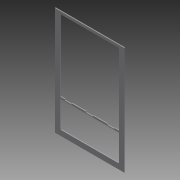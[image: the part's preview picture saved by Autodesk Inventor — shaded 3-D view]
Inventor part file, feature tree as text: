
AUTODESK INVENTOR PART (.ipt)
format: ipt  version: 2011 (Build 150239000, 239)  size: 1,064,960 bytes
history: native  units: in
note: dims shown in document units (in); Inventor stores cm internally (conversion verified against a paired STEP export)
features: extrude x29, sketch x29, fillet x4
ambient origin geometry x8: Origin, YZ Plane, XZ Plane, XY Plane, X Axis, Y Axis, Z Axis, Center Point
bodies: Solid1 (feature_tree)
feature tree (62):
  extrude  "Extrusion1"  Depth=35.0in
  extrude  "Extrusion2"  Depth=1.5in
  extrude  "Extrusion3"  Depth=0.75in
  extrude  "Extrusion4"  Depth=2.25in
  fillet  "Fillet1"  Radius=0.156in
  extrude  "Extrusion5"  Depth=0.25in TaperAngle=0.0deg
  extrude  "Extrusion6"  Depth=3.0in
  extrude  "Extrusion7"  Depth=1.0in
  extrude  "Extrusion8"  Depth=0.25in TaperAngle=0.0deg
  extrude  "Extrusion9"  Depth=3.5in
  extrude  "Extrusion10"  Depth=3.5in
  extrude  "Extrusion11"  Depth=0.25in TaperAngle=0.0deg
  extrude  "Extrusion12"  Depth=0.25in
  extrude  "Extrusion13"  Depth=1.0in
  extrude  "Extrusion14"  Depth=1.0in
  extrude  "Extrusion15"  Depth=1.0in
  extrude  "Extrusion16"  Depth=1.0in
  extrude  "Extrusion17"  Depth=1.0in
  extrude  "Extrusion18"  Depth=1.0in
  extrude  "Extrusion19"  Depth=1.0in
  extrude  "Extrusion20"  Depth=1.0in
  extrude  "Extrusion21"  Depth=1.0in
  fillet  "Fillet2"  Radius=1.0in
  extrude  "Extrusion22"  Depth=0.25in TaperAngle=0.0deg
  extrude  "Extrusion23"  Depth=2.0in
  extrude  "Extrusion24"  Depth=2.0in
  extrude  "Extrusion25"  Depth=2.0in
  extrude  "Extrusion26"  Depth=2.0in
  fillet  "Fillet3"  Radius=2.0in
  extrude  "Extrusion27"  Depth=2.0in
  extrude  "Extrusion28"  Depth=2.0in
  fillet  "Fillet4"  Radius=2.0in
  extrude  "Extrusion29"  Depth=2.0in
  sketch  "Sketch1"  dims[d0=19.5in d1=35.0in]
  sketch  "Sketch2"  dims[d2=0.25in d3=0.0in d4=1.5in]
  sketch  "Sketch3"  dims[d5=3.0in d6=0.75in]
  sketch  "Sketch4"  dims[d7=0.75in d8=2.25in d9=0.156in]
  sketch  "Sketch5"  dims[d10=0.156in d11=0.25in d12=0.0in]
  sketch  "Sketch6"  dims[d13=1.5in d14=3.0in]
  sketch  "Sketch7"  dims[d15=1.5in d16=1.0in]
  sketch  "Sketch8"  dims[d17=32.25in d18=0.25in d19=0.0in]
  sketch  "Sketch9"  dims[d20=2.0in d21=3.5in]
  sketch  "Sketch10"  dims[d22=2.0in d23=3.5in]
  sketch  "Sketch11"  dims[d24=1.5in d25=0.25in d26=0.0in]
  sketch  "Sketch12"  dims[d27=0.25in d28=0.25in]
  sketch  "Sketch13"  dims[d29=0.25in d30=1.0in]
  sketch  "Sketch14"  dims[d31=1.0in d32=1.0in]
  sketch  "Sketch15"  dims[d33=1.0in d34=1.0in]
  sketch  "Sketch16"  dims[d35=1.0in d36=1.0in]
  sketch  "Sketch17"  dims[d37=1.0in d38=1.0in]
  sketch  "Sketch18"  dims[d39=1.0in d40=1.0in]
  sketch  "Sketch19"  dims[d41=1.0in d42=1.0in]
  sketch  "Sketch20"  dims[d43=1.0in d44=1.0in]
  sketch  "Sketch21"  dims[d45=1.0in d46=1.0in d47=1.0in]
  sketch  "Sketch22"  dims[d48=1.0in d49=0.25in d50=0.0in]
  sketch  "Sketch23"  dims[d51=2.0in d52=2.0in]
  sketch  "Sketch24"  dims[d53=2.0in d54=2.0in]
  sketch  "Sketch25"  dims[d55=2.0in d56=2.0in]
  sketch  "Sketch26"  dims[d57=2.0in d58=2.0in d59=2.0in]
  sketch  "Sketch27"  dims[d60=2.0in d61=2.0in]
  sketch  "Sketch28"  dims[d62=2.0in d63=2.0in d64=2.0in]
  sketch  "Sketch29"  dims[d65=2.0in d66=2.0in d67=2.0in d68=0.25in d69=0.0in d70=0.25in d71=0.0in d72=0.25in d73=0.0in d74=0.75in d75=0.25in d76=0.75in d77=0.25in d78=2.0in d79=2.0in d80=2.0in d81=2.0in d82=2.0in d83=2.0in d84=2.0in d85=2.0in d86=0.25in d87=0.0in d88=2.0in d89=2.0in d90=2.0in d91=2.0in d92=0.25in d93=0.0in d94=2.0in d95=2.0in d96=0.25in d97=0.0in d98=0.25in d99=0.25in d100=0.0in d101=9.0in d102=0.5in d103=0.75in d104=1.0in d105=0.0in d106=1.0in d107=0.0in d108=9.25in d109=0.25in d110=2.0in d111=0.25in d112=2.0in d113=4.0in d114=2.0in d115=1.0in d116=0.0in d117=0.25in d118=0.0in d119=0.5in d120=2.5in d121=0.5in d122=2.5in d123=0.156in d124=0.156in d125=0.25in d126=0.0in d127=1.0in d128=0.0in d129=1.0in d130=0.0in d131=0.25in d132=0.0in d133=0.25in d134=0.0in d135=0.25in d136=8.25in d137=1.0in d138=2.0in d139=0.25in d140=4.0in d141=2.0in d142=4.0in d143=2.0in d144=0.25in d145=0.0in d146=0.25in d147=0.0in d148=0.25in d149=0.0in d150=3.86in d151=1.0in d152=0.0in d153=0.25in d154=1.5in d155=0.25in d156=0.0in d157=0.25in d158=0.25in d159=0.0in d160=0.25in d161=0.25in d162=0.0in d163=0.25in d164=0.75in d165=1.0in d166=0.0in]
